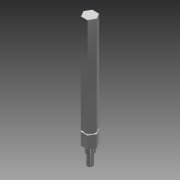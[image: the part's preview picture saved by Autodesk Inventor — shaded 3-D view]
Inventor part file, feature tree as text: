
AUTODESK INVENTOR PART (.ipt)
format: ipt  version: 2016 SP1 (Build 200210100, 210)  size: 105,984 bytes
history: native  units: in
note: dims shown in document units (in); Inventor stores cm internally (conversion verified against a paired STEP export)
features: chamfer x1
ambient origin geometry x8: Origin, YZ Plane, XZ Plane, XY Plane, X Axis, Y Axis, Z Axis, Center Point
bodies: Solid1 (feature_tree)
feature tree (1):
  chamfer  "Chamfer1"  [1 undecoded]
note: 1 required parameter value undecoded (feature->parameter linkage not recoverable at this tier; creation-order binding heuristic only, values carry confidence <= 0.55)
